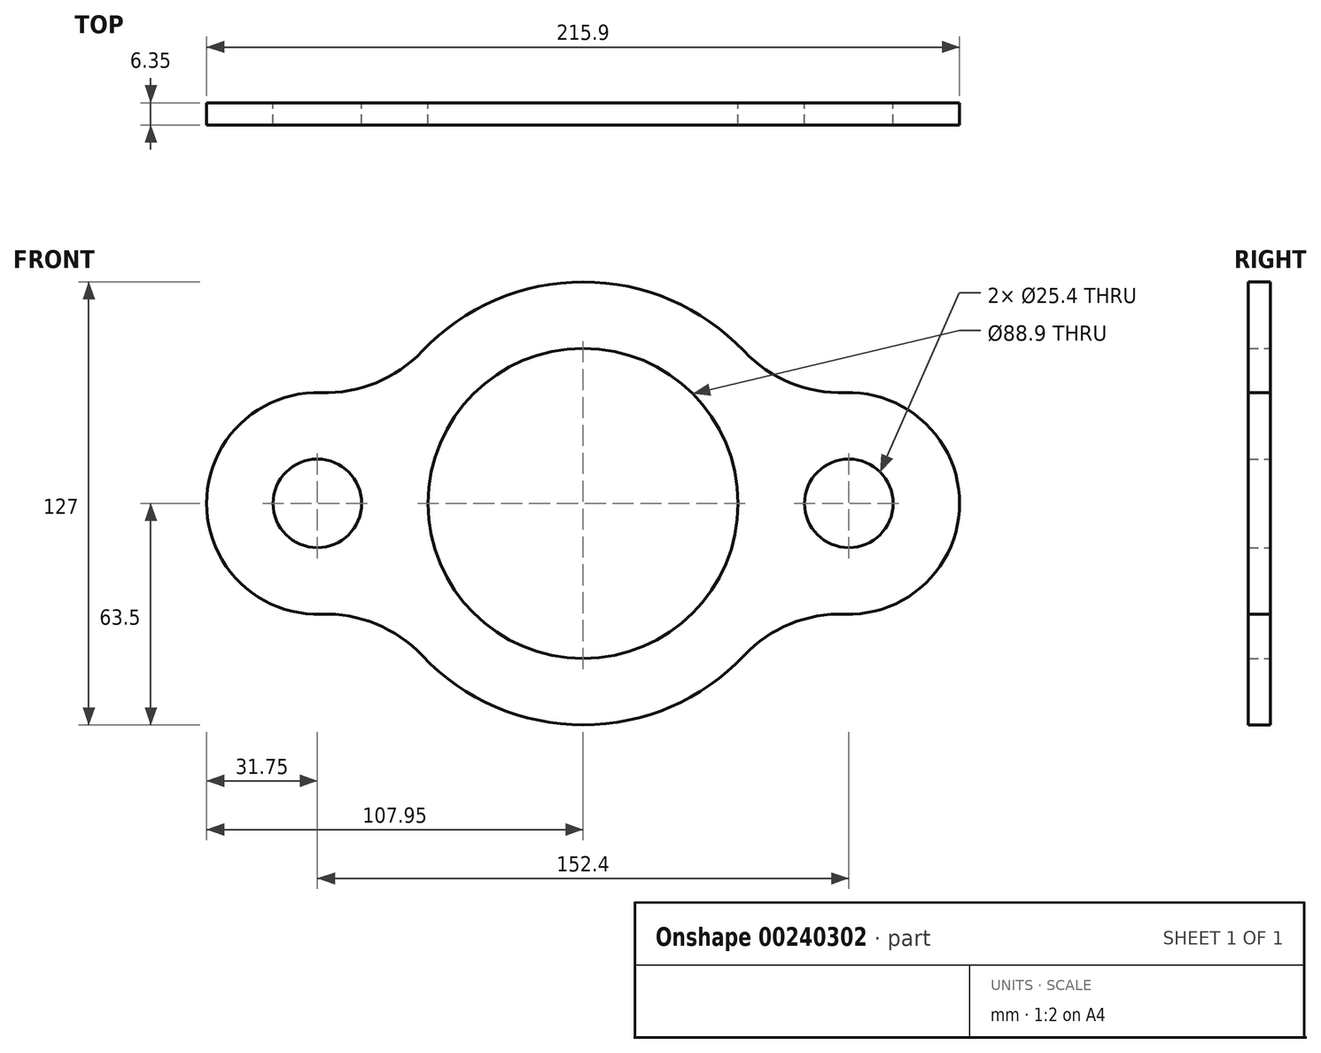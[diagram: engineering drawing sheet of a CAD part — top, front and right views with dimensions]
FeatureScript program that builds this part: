
annotation { "Feature Type Name" : "Feature", "Feature Type Description" : "" }
export const myFeature = defineFeature(function(context is Context, id is Id, definition is map)
    precondition{}
    {
        {
            var Q0;
            Q0=qCreatedBy(makeId("Front.planeOp"),FACE);
            var sketch = newSketch(context, id + "F0", { "sketchPlane" : qUnion([Q0])});
            skArc(sketch, "E0", {"start": v(-46.14, -43.63) * mm, "mid": v(0, -63.5) * mm, "end": v(46.14, -43.63) * mm});
            skCircle(sketch, "E1", {"center": v(0, 0) * mm, "radius": 44.45 * mm});
            skCircle(sketch, "E2", {"center": v(-76.2, 0) * mm, "radius": 12.7 * mm});
            skCircle(sketch, "E3", {"center": v(76.2, 0) * mm, "radius": 12.7 * mm});
            skArc(sketch, "E4", {"start": v(-75.12, 31.73) * mm, "mid": v(-107.95, 0) * mm, "end": v(-75.12, -31.73) * mm});
            skArc(sketch, "E5", {"start": v(75.12, -31.73) * mm, "mid": v(107.95, 0) * mm, "end": v(75.12, 31.73) * mm});
            skPoint(sketch, "E6.visualSharp", {"position": v(-57.94, -25.98) * mm});
            skArc(sketch, "E6.filletArc", {"start": v(-46.14, -43.63) * mm, "mid": v(-59.35, -34.56) * mm, "end": v(-75.12, -31.73) * mm});
            skArc(sketch, "E7.trimOffspring", {"start": v(46.14, 43.63) * mm, "mid": v(0, 63.5) * mm, "end": v(-46.14, 43.63) * mm});
            skPoint(sketch, "E8.visualSharp", {"position": v(57.94, -25.98) * mm});
            skArc(sketch, "E8.filletArc", {"start": v(75.12, -31.73) * mm, "mid": v(59.35, -34.56) * mm, "end": v(46.14, -43.63) * mm});
            skPoint(sketch, "E9.visualSharp", {"position": v(57.94, 25.98) * mm});
            skArc(sketch, "E9.filletArc", {"start": v(46.14, 43.63) * mm, "mid": v(59.35, 34.56) * mm, "end": v(75.12, 31.73) * mm});
            skPoint(sketch, "E10.visualSharp", {"position": v(-57.94, 25.98) * mm});
            skArc(sketch, "E10.filletArc", {"start": v(-75.12, 31.73) * mm, "mid": v(-59.35, 34.56) * mm, "end": v(-46.14, 43.63) * mm});
            skSolve(sketch);
        }
        {
            var Q0;
            Q0 = qSketchRegion(id + "F0", true);
            extrude(context, id + "F1", {"entities" : qUnion([Q0]), "depth" : 6.35 * mm});
        }
    });
